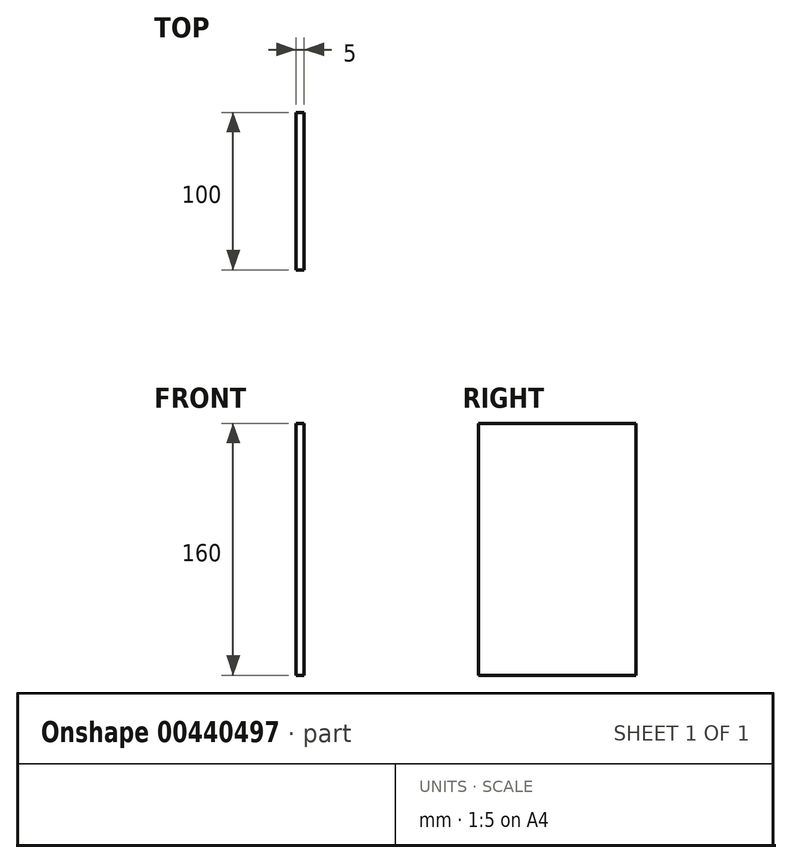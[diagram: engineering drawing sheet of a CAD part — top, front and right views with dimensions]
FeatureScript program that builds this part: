
annotation { "Feature Type Name" : "Feature", "Feature Type Description" : "" }
export const myFeature = defineFeature(function(context is Context, id is Id, definition is map)
    precondition{}
    {
        {
            var Q0;
            Q0=qCreatedBy(makeId("Top.planeOp"),FACE);
            var sketch = newSketch(context, id + "F0", { "sketchPlane" : qUnion([Q0])});
            skLineSegment(sketch, "E0.bottom", {"start": v(-2.5, 50) * mm, "end": v(2.5, 50) * mm});
            skLineSegment(sketch, "E0.top", {"start": v(-2.5, -50) * mm, "end": v(2.5, -50) * mm});
            skLineSegment(sketch, "E0.left", {"start": v(-2.5, 50) * mm, "end": v(-2.5, -50) * mm});
            skLineSegment(sketch, "E0.right", {"start": v(2.5, 50) * mm, "end": v(2.5, -50) * mm});
            skPoint(sketch, "E0.middle", {"position": v(0, 0) * mm});
            skSolve(sketch);
        }
        {
            var Q0;
            Q0 = qSketchRegion(id + "F0", true);
            extrude(context, id + "F1", {"entities" : qUnion([Q0]), "depth" : 160 * mm});
        }
    });
